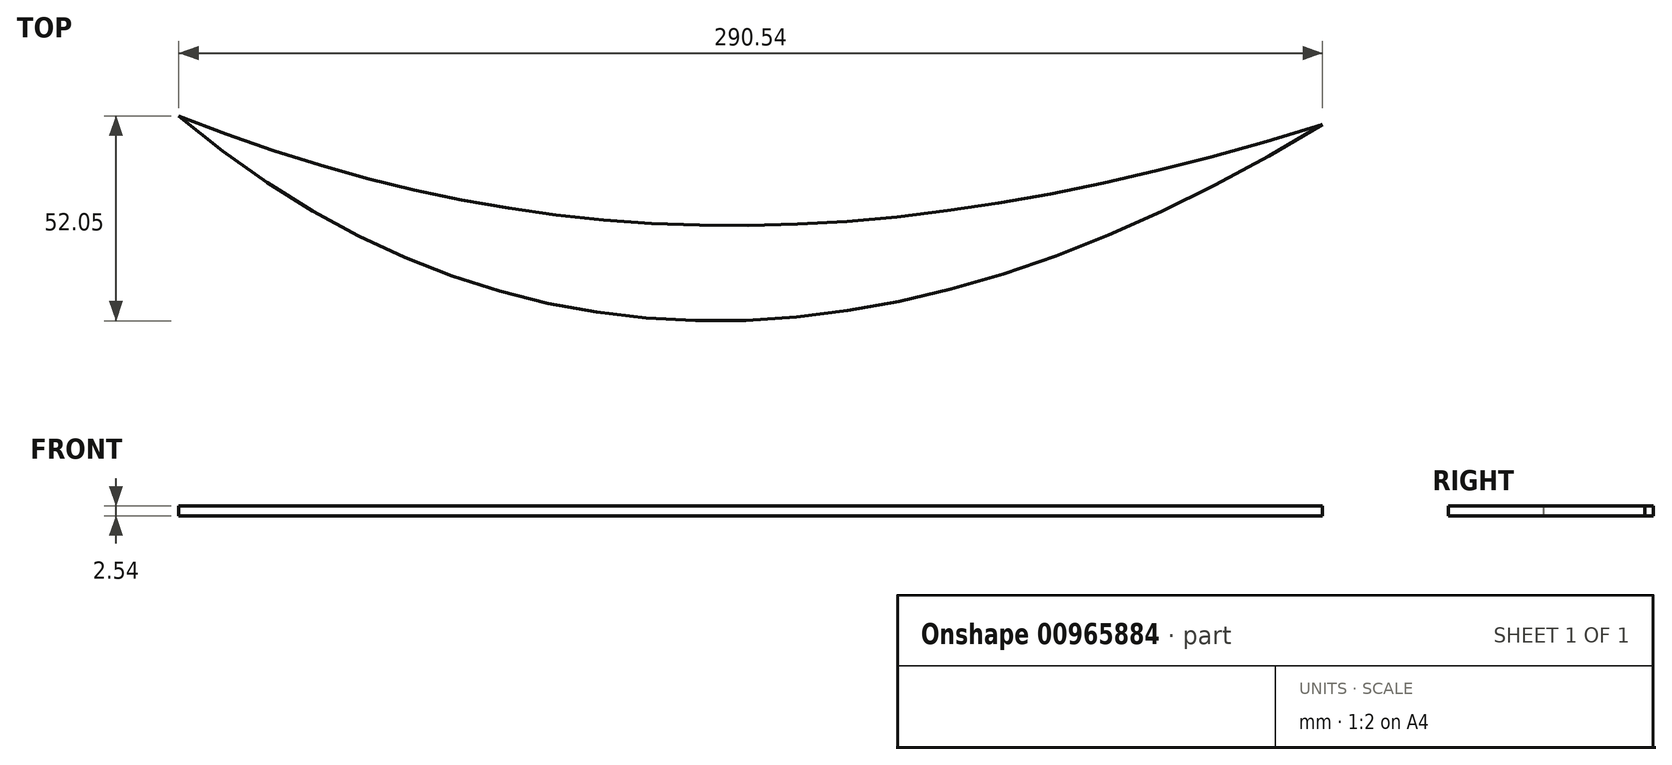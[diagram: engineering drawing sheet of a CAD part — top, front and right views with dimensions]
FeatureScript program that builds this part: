
annotation { "Feature Type Name" : "Feature", "Feature Type Description" : "" }
export const myFeature = defineFeature(function(context is Context, id is Id, definition is map)
    precondition{}
    {
        {
            var Q0;
            Q0=qCreatedBy(makeId("Top.planeOp"),FACE);
            var sketch = newSketch(context, id + "F0", { "sketchPlane" : qUnion([Q0])});
            skFitSpline(sketch, "E0", {"points": [v(-137.54, 36.75) * mm, v(153, 34.62) * mm], "startDerivative": vector(254.3, -214.3) * mm, "endDerivative": vector(315.06, 193.52) * mm});
            skFitSpline(sketch, "E1", {"points": [v(-137.54, 36.75) * mm, v(153, 34.62) * mm], "startDerivative": vector(276.68, -110.25) * mm, "endDerivative": vector(331.06, 103.86) * mm});
            skSolve(sketch);
        }
        {
            var Q0;
            Q0=makeQuery(id+"F0.imprint","IMPRINT",FACE,{"disambiguationData":[TD([[makeQuery(id+"F0.imprint","IMPRINT",EDGE,{"derivedFrom":sQuery(id+"F0.wireOp",EDGE,"E0")}),1.0]])]});
            extrude(context, id + "F1", {"entities" : qUnion([Q0]), "depth" : 2.54 * mm, "offsetDistance" : 25.4 * mm});
        }
    });
